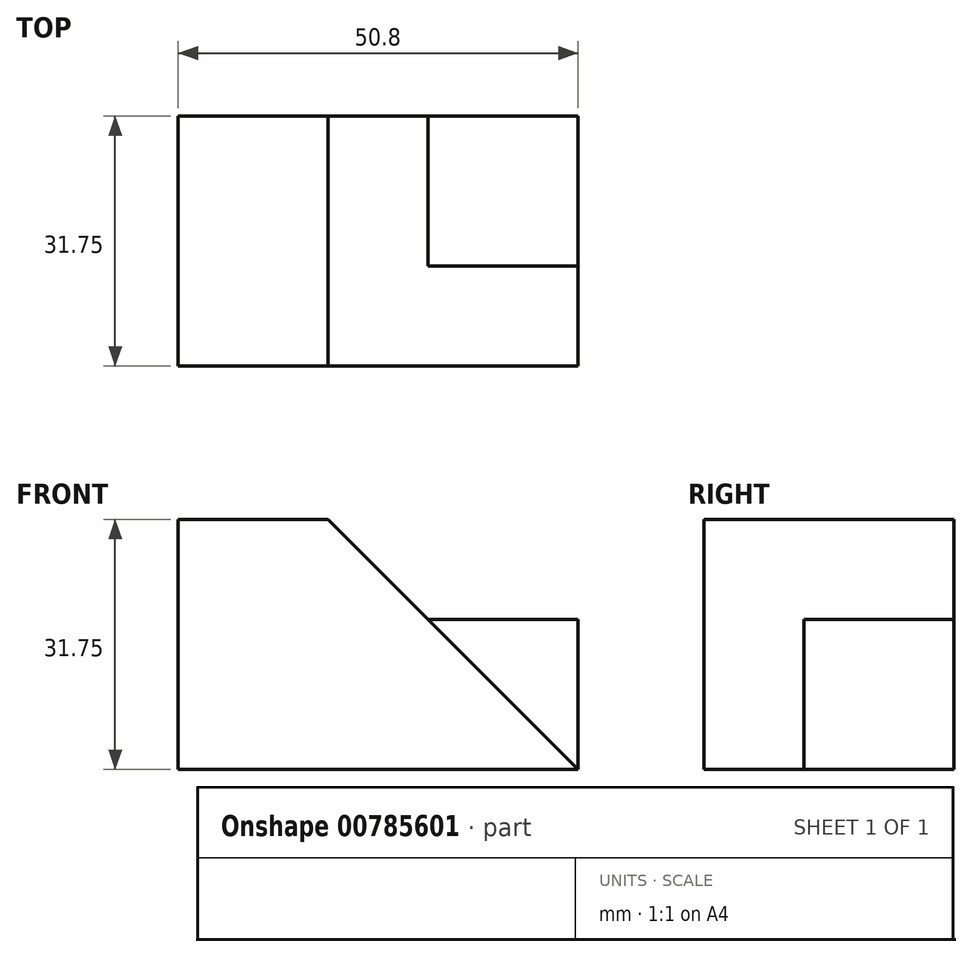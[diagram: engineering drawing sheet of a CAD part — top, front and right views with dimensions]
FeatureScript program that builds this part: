
annotation { "Feature Type Name" : "Feature", "Feature Type Description" : "" }
export const myFeature = defineFeature(function(context is Context, id is Id, definition is map)
    precondition{}
    {
        {
            var Q0;
            Q0=qCreatedBy(makeId("Front.planeOp"),FACE);
            var sketch = newSketch(context, id + "F0", { "sketchPlane" : qUnion([Q0])});
            skLineSegment(sketch, "E0", {"start": v(0, 0) * mm, "end": v(50.8, 0) * mm});
            skLineSegment(sketch, "E1", {"start": v(50.8, 0) * mm, "end": v(50.8, 31.75) * mm});
            skLineSegment(sketch, "E2", {"start": v(50.8, 31.75) * mm, "end": v(0, 31.75) * mm});
            skLineSegment(sketch, "E3", {"start": v(0, 31.75) * mm, "end": v(0, 0) * mm});
            skSolve(sketch);
        }
        {
            var Q0;
            Q0 = qSketchRegion(id + "F0", true);
            extrude(context, id + "F1", {"entities" : qUnion([Q0]), "depth" : 31.75 * mm, "offsetDistance" : 25.4 * mm});
        }
        {
            var Q0;
            Q0=makeQuery(id+"F1.opExtrude","CAP_FACE",FACE,{"disambiguationData":[OSD([sQuery(id+"F0.wireOp",EDGE,"E0"),sQuery(id+"F0.wireOp",EDGE,"E1"),sQuery(id+"F0.wireOp",EDGE,"E2"),sQuery(id+"F0.wireOp",EDGE,"E3")])],"isStart":false});
            var sketch = newSketch(context, id + "F2", { "sketchPlane" : qUnion([Q0])});
            skLineSegment(sketch, "E4", {"start": v(0, 0) * mm, "end": v(0, 31.75) * mm});
            skLineSegment(sketch, "E5", {"start": v(0, 31.75) * mm, "end": v(19.05, 31.75) * mm});
            skLineSegment(sketch, "E6", {"start": v(19.05, 31.75) * mm, "end": v(50.8, 0) * mm});
            skLineSegment(sketch, "E7", {"start": v(50.8, 0) * mm, "end": v(0, 0) * mm});
            skSolve(sketch);
        }
        {
            var Q0;
            {var subQ0=sQuery(id+"F2.wireOp",EDGE,"E6");Q0=makeQuery(id+"F2.imprint","IMPRINT",FACE,{"disambiguationData":[TD([[makeQuery(id+"F2.imprint","IMPRINT",EDGE,{"derivedFrom":subQ0}),1.0]])]});}
            extrude(context, id + "F3", {"entities" : qUnion([Q0]), "operationType" : NewBodyOperationType.REMOVE, "oppositeDirection" : true, "depth" : 12.7 * mm, "offsetDistance" : 25.4 * mm});
        }
        {
            var Q0;
            Q0=makeQuery(id+"F3.boolean.opBoolean","COPY",FACE,{"derivedFrom":makeQuery(id+"F3.opExtrude","CAP_FACE",FACE,{"disambiguationData":[OSD([sQuery(id+"F0.wireOp",EDGE,"E1"),sQuery(id+"F0.wireOp",EDGE,"E2"),sQuery(id+"F2.wireOp",EDGE,"E6")])],"isStart":false})});
            var sketch = newSketch(context, id + "F4", { "sketchPlane" : qUnion([Q0])});
            skLineSegment(sketch, "E8", {"start": v(50.8, 31.75) * mm, "end": v(50.8, 19.05) * mm});
            skLineSegment(sketch, "E9", {"start": v(50.8, 19.05) * mm, "end": v(31.75, 19.05) * mm});
            skLineSegment(sketch, "E10", {"start": v(31.75, 19.05) * mm, "end": v(19.05, 31.75) * mm});
            skLineSegment(sketch, "E11", {"start": v(19.05, 31.75) * mm, "end": v(50.8, 31.75) * mm});
            skSolve(sketch);
        }
        {
            var Q0;
            Q0=makeQuery(id+"F4.imprint","IMPRINT",FACE,{"disambiguationData":[TD([[makeQuery(id+"F4.imprint","IMPRINT",EDGE,{"derivedFrom":sQuery(id+"F4.wireOp",EDGE,"E8")}),1.0]])]});
            extrude(context, id + "F5", {"entities" : qUnion([Q0]), "operationType" : NewBodyOperationType.REMOVE, "oppositeDirection" : true, "depth" : 19.05 * mm, "offsetDistance" : 25.4 * mm});
        }
    });
